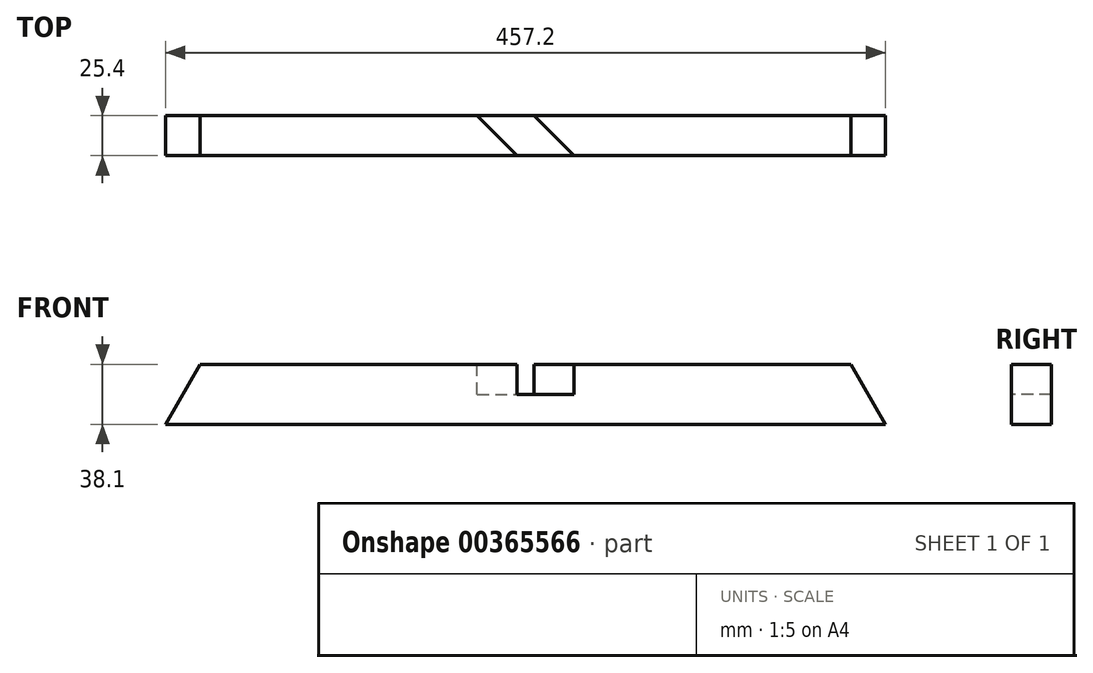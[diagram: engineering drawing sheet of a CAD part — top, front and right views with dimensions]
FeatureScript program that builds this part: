
annotation { "Feature Type Name" : "Feature", "Feature Type Description" : "" }
export const myFeature = defineFeature(function(context is Context, id is Id, definition is map)
    precondition{}
    {
        {
            var Q0;
            Q0=qCreatedBy(makeId("Front.planeOp"),FACE);
            var sketch = newSketch(context, id + "F0", { "sketchPlane" : qUnion([Q0])});
            skLineSegment(sketch, "E0.bottom", {"start": v(0, 0) * mm, "end": v(457.2, 0) * mm});
            skLineSegment(sketch, "E0.top", {"start": v(22, 38.1) * mm, "end": v(435.2, 38.1) * mm});
            skLineSegment(sketch, "E1", {"start": v(0, 0) * mm, "end": v(22, 38.1) * mm});
            skLineSegment(sketch, "E2", {"start": v(457.2, 0) * mm, "end": v(435.2, 38.1) * mm});
            skSolve(sketch);
        }
        {
            var Q0;
            Q0=makeQuery(id+"F0.imprint","IMPRINT",FACE,{"disambiguationData":[TD([[makeQuery(id+"F0.imprint","IMPRINT",EDGE,{"derivedFrom":sQuery(id+"F0.wireOp",EDGE,"E0.bottom")}),1.0]])]});
            extrude(context, id + "F1", {"entities" : qUnion([Q0]), "depth" : 25.4 * mm});
        }
        {
            var Q0;
            Q0=makeQuery(id+"F1.opExtrude","SWEPT_FACE",FACE,{"disambiguationData":[OSD([sQuery(id+"F0.wireOp",EDGE,"E0.top")])]});
            var sketch = newSketch(context, id + "F2", { "sketchPlane" : qUnion([Q0])});
            skLineSegment(sketch, "E3", {"start": v(197.94, 0) * mm, "end": v(223.34, -25.4) * mm});
            skLineSegment(sketch, "E4", {"start": v(223.34, -25.4) * mm, "end": v(259.26, -25.4) * mm});
            skLineSegment(sketch, "E5", {"start": v(259.26, -25.4) * mm, "end": v(233.86, 0) * mm});
            skLineSegment(sketch, "E6", {"start": v(233.86, 0) * mm, "end": v(197.94, 0) * mm});
            skCircle(sketch, "E7", {"center": v(228.6, -12.7) * mm, "radius": 12.7 * mm, "construction": true});
            skSolve(sketch);
        }
        {
            var Q0;
            Q0=makeQuery(id+"F2.imprint","IMPRINT",FACE,{"disambiguationData":[TD([[makeQuery(id+"F2.imprint","IMPRINT",EDGE,{"derivedFrom":sQuery(id+"F2.wireOp",EDGE,"E3")}),1.0]])]});
            extrude(context, id + "F3", {"entities" : qUnion([Q0]), "operationType" : NewBodyOperationType.REMOVE, "depth" : -19.05 * mm});
        }
    });
